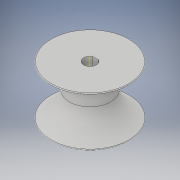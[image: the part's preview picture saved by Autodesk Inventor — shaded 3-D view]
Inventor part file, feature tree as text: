
AUTODESK INVENTOR PART (.ipt)
format: ipt  version: 2019 (Build 230136000, 136)  size: 176,128 bytes
history: native  units: in
note: dims shown in document units (in); Inventor stores cm internally (conversion verified against a paired STEP export)
features: sketch x2, revolve x1, extrude x1, mirror x1, fillet x1
ambient origin geometry x8: Origin, YZ Plane, XZ Plane, XY Plane, X Axis, Y Axis, Z Axis, Center Point
bodies: Body1 (feature_tree)
feature tree (6):
  revolve  "Revolution1"  [1 undecoded]
  extrude  "Extrusion1"  TaperAngle=90.0deg  [1 undecoded]
  mirror  "Mirror2"
  fillet  "Fillet1"  Radius=0.23in
  sketch  "Sketch4"  dims[d18=0.375in d19=0.45in]
  sketch  "Sketch5"  dims[d20=0.75in d21=90.0deg d22=0.23in d23=0.101in d24=1.0in d25=0.0in d26=0.01in]
note: 2 required parameter values undecoded (feature->parameter linkage not recoverable at this tier; creation-order binding heuristic only, values carry confidence <= 0.55)